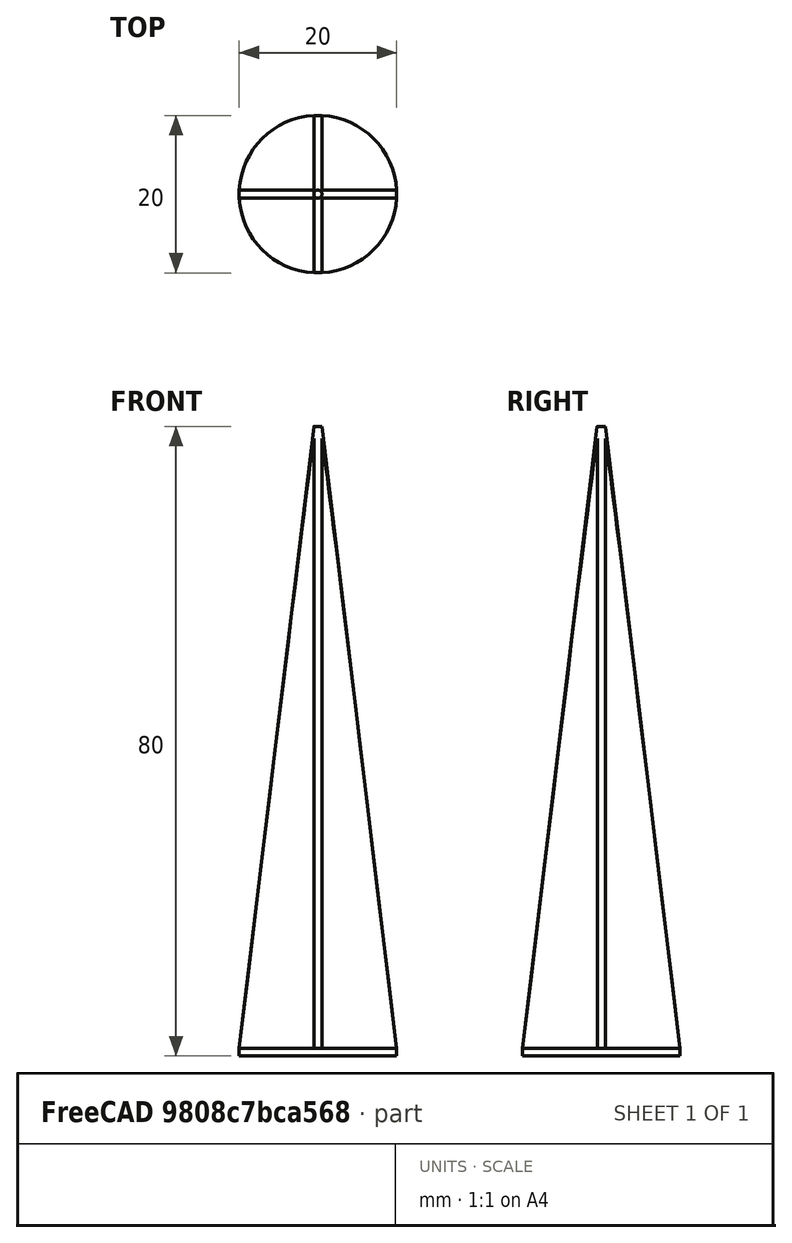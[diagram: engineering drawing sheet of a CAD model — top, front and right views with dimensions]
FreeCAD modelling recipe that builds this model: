
FCSTD DOCUMENT  (FreeCAD 1.1R1.1.0)
Label: GroundAnchor01
License: All rights reserved
LicenseURL: http://en.wikipedia.org/wiki/All_rights_reserved
objects: Part::Box×2, Part::MultiFuse×2, Spreadsheet::Sheet×1, Part::Cylinder×1, Part::Cone×1, Part::MultiCommon×1
note: 7 computed .brp shape members not serialized (recipe doc carries the construction recipe); baked Part::Feature solids carry a one-line shape summary decoded from their .brp

FEATURE [Spreadsheet::Sheet] Spreadsheet  label="Params"
  cells = A2='Plate diameter; B2(plate_dia)=20; A3='Length; B3(len)=80; A4='Thickness; B4(thickness)=1
FEATURE [Part::Cylinder] Cylinder
  Angle = 360
  AttacherType = Attacher::AttachEngine3D
  FirstAngle = 0
  Height = 1
  Radius = 10
  SecondAngle = 0
  expr: Height = <<Params>>.thickness
  expr: Radius = <<Params>>.plate_dia / 2
FEATURE [Part::Cone] Cone
  Angle = 360
  AttacherType = Attacher::AttachEngine3D
  Height = 80
  Placement = pos=(0,0,1) rot=(0,0,1;0rad)
  Radius1 = 10
  Radius2 = 0.4
  expr: .Placement.Base.z = <<Params>>.thickness
  expr: Height = <<Params>>.len
  expr: Radius1 = <<Params>>.plate_dia / 2
FEATURE [Part::Box] Box  label="Cube"
  AttacherType = Attacher::AttachEngine3D
  Height = 80
  Length = 20
  Placement = pos=(-10,-0.5,0) rot=(0,0,1;0rad)
  Width = 1
  expr: .Placement.Base.x = -<<Params>>.plate_dia / 2
  expr: .Placement.Base.y = -<<Params>>.thickness / 2
  expr: Height = <<Params>>.len
  expr: Length = <<Params>>.plate_dia
  expr: Width = <<Params>>.thickness
FEATURE [Part::Box] Box001  label="Cube001"
  AttacherType = Attacher::AttachEngine3D
  Height = 80
  Length = 20
  Placement = pos=(0.5,-10,0) rot=(0,0,1;1.5708rad)
  Width = 1
  expr: .Placement.Base.x = <<Params>>.thickness / 2
  expr: .Placement.Base.y = -<<Params>>.plate_dia / 2
  expr: Height = <<Params>>.len
  expr: Length = <<Params>>.plate_dia
  expr: Width = <<Params>>.thickness
FEATURE [Part::MultiFuse] Fusion
  Shapes = -> [Box,Box001]
FEATURE [Part::MultiCommon] Common
  Behavior = 0
  Shapes = -> [Cone,Fusion]
FEATURE [Part::MultiFuse] Fusion001  label="GroundAnchor"
  Shapes = -> [Common,Cylinder]
